# Revit family: Basin-One_Station-Acorn-Kurve®, Meridian-3793
name_source: partatom
category: Plumbing Fixtures
units: mm (PartAtom-declared; Revit-internal decimal feet)

## family parameters
Cut with Voids When Loaded = No
Host = Face
OmniClass Number = 23.45.05.14.14
OmniClass Title = Sinks/Lavatories
Part Type = Normal
Room Calculation Point = No
Round Connector Dimension = Use Diameter
Shared = Yes

## types (1)
- 3793
    ADA Compliant = Yes
    Assembly Code = D2010300
    Bowl Shape = Curve
    CW Connection = Yes
    CWFU = 1.5
    Compliance Certifications = Complies with IAPMO IGC 156, CSA B45 Series, ASME A112.18.1/CSA B125.1
    Countertop, Basin and Sprayhead Shelf Material = Polymer Resin Corterra-Acorn-Solid Surface OCC11M
    DV - Liquid / Lotion Soap Dispenser = Yes
    Default Elevation = 34"
    Description = Two Station, Cast Solid Surface Kurve® Wash Basin
    Faucet Material = Metal-Acorn-Stainless Steel
    Flow Rate = 0.5 GPM
    H - Hand Operation = No
    HW Connection = Yes
    HWFU = 1.5
    Height = 21"
    Inlet Connection Diameter = 1/2"
    Inlet Connection Height = 24"
    Inlet Connection Width = 9"
    Installation Type = Wall Mounted
    KP2 Kick Plate Must Specify Rim Height = No
    LWP - Less Waste Piping = No
    Length = 84"
    Manufacturer = Acorn
    Material = Polymer Resin Corterra-Acorn-Solid Surface OCC11M
    Model = 3793
    Operating Range = 30 PSI - 100 PSI
    P-Trap Enclosure Material = Stainless Steel-Acorn-Satin
    PPZ - Programmable Piezo Push button Electronic Metering = No
    Product Documentation Link = https://www.acorneng.com
    Product Page URL = https://www.acorneng.com
    SO - Sensor Operated = No
    SO-BAT- Sensor Operation (Batteries Not Included) = No
    ST - Single Temperature Valve = No
    Sensor Material = Plastic-Acorn-Black
    URL = https://www.acorneng.com
    Vent Connection = No
    WFU = 2
    Warranty Documentation Link = https://www.acorneng.com
    Waste Connection = Yes
    Waste Connection Diameter = 1 1/2"
    Waste Connection Height = 25"
    Waste Connection Width = 3"
    Width = 20 3/4"

## geometry (parser evidence)
native form markers: Sweep x3
no freeform markers — native parametric forms only
